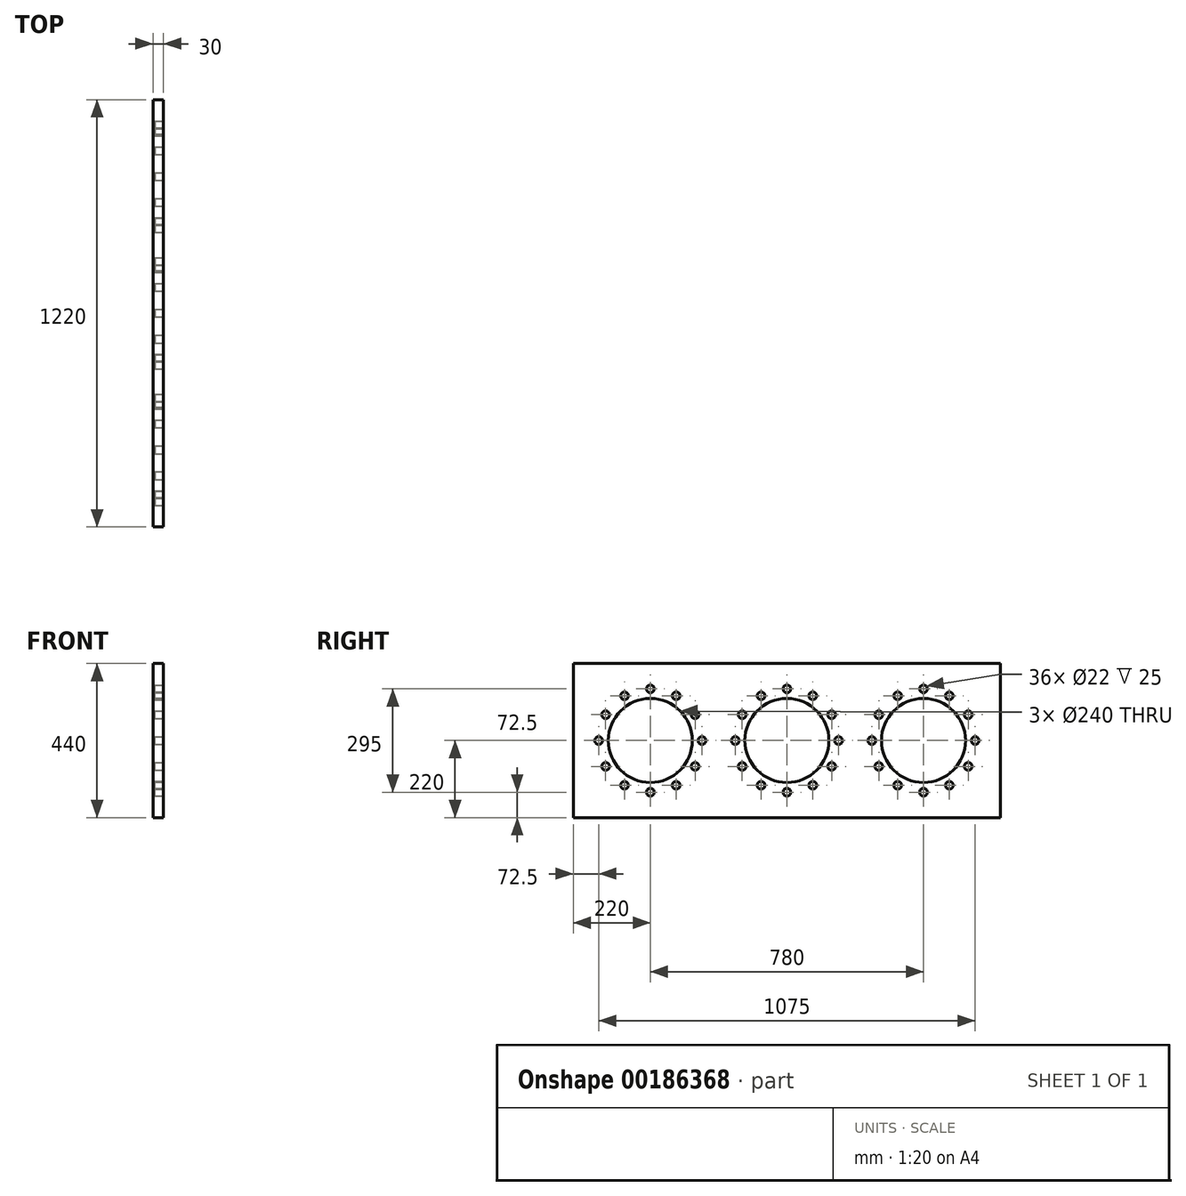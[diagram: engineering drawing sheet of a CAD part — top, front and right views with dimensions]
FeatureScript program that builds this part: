
annotation { "Feature Type Name" : "Feature", "Feature Type Description" : "" }
export const myFeature = defineFeature(function(context is Context, id is Id, definition is map)
    precondition{}
    {
        {
            var Q0;
            Q0=qCreatedBy(makeId("Right.planeOp"),FACE);
            var sketch = newSketch(context, id + "F0", { "sketchPlane" : qUnion([Q0])});
            skCircle(sketch, "E0", {"center": v(610, 220) * mm, "radius": 120 * mm});
            skCircle(sketch, "E1", {"center": v(220, 220) * mm, "radius": 120 * mm});
            skCircle(sketch, "E2", {"center": v(1000, 220) * mm, "radius": 120 * mm});
            skLineSegment(sketch, "E3.bottom", {"start": v(0, 0) * mm, "end": v(1220, 0) * mm});
            skLineSegment(sketch, "E3.top", {"start": v(0, 440) * mm, "end": v(1220, 440) * mm});
            skLineSegment(sketch, "E3.left", {"start": v(0, 0) * mm, "end": v(0, 440) * mm});
            skLineSegment(sketch, "E3.right", {"start": v(1220, 0) * mm, "end": v(1220, 440) * mm});
            skLineSegment(sketch, "E4", {"start": v(0, 220) * mm, "end": v(1220, 220) * mm, "construction": true});
            skSolve(sketch);
        }
        {
            var Q0;
            Q0=makeQuery(id+"F0.imprint","IMPRINT",FACE,{"disambiguationData":[TD([[makeQuery(id+"F0.imprint","IMPRINT",EDGE,{"derivedFrom":sQuery(id+"F0.wireOp",EDGE,"E0")}),-1.0]])]});
            extrude(context, id + "F1", {"entities" : qUnion([Q0]), "depth" : 30 * mm});
        }
        {
            var Q0;
            Q0=makeQuery(id+"F1.opExtrude","CAP_FACE",FACE,{"disambiguationData":[OSD([sQuery(id+"F0.wireOp",EDGE,"E0"),sQuery(id+"F0.wireOp",EDGE,"E1"),sQuery(id+"F0.wireOp",EDGE,"E2"),sQuery(id+"F0.wireOp",EDGE,"E3.bottom"),sQuery(id+"F0.wireOp",EDGE,"E3.top"),sQuery(id+"F0.wireOp",EDGE,"E3.left"),sQuery(id+"F0.wireOp",EDGE,"E3.right")])],"isStart":false});
            var sketch = newSketch(context, id + "F2", { "sketchPlane" : qUnion([Q0])});
            skCircle(sketch, "E5", {"center": v(367.5, 220) * mm, "radius": 11 * mm});
            skCircle(sketch, "E6.1.0", {"center": v(347.74, 146.25) * mm, "radius": 11 * mm});
            skCircle(sketch, "E6.2.0", {"center": v(293.75, 92.26) * mm, "radius": 11 * mm});
            skCircle(sketch, "E6.3.0", {"center": v(220, 72.5) * mm, "radius": 11 * mm});
            skCircle(sketch, "E6.4.0", {"center": v(146.25, 92.26) * mm, "radius": 11 * mm});
            skCircle(sketch, "E6.5.0", {"center": v(92.26, 146.25) * mm, "radius": 11 * mm});
            skCircle(sketch, "E6.6.0", {"center": v(72.5, 220) * mm, "radius": 11 * mm});
            skCircle(sketch, "E6.7.0", {"center": v(92.26, 293.75) * mm, "radius": 11 * mm});
            skCircle(sketch, "E6.8.0", {"center": v(146.25, 347.74) * mm, "radius": 11 * mm});
            skCircle(sketch, "E6.9.0", {"center": v(220, 367.5) * mm, "radius": 11 * mm});
            skCircle(sketch, "E6.10.0", {"center": v(293.75, 347.74) * mm, "radius": 11 * mm});
            skCircle(sketch, "E6.11.0", {"center": v(347.74, 293.75) * mm, "radius": 11 * mm});
            skPoint(sketch, "E6.center", {"position": v(220, 220) * mm});
            skLineSegment(sketch, "E6.anchor1", {"start": v(220, 220) * mm, "end": v(367.5, 220) * mm, "construction": true});
            skLineSegment(sketch, "E6.anchor2", {"start": v(220, 220) * mm, "end": v(347.74, 293.75) * mm, "construction": true});
            skCircle(sketch, "E7", {"center": v(757.5, 220) * mm, "radius": 11 * mm});
            skCircle(sketch, "E8.1.0", {"center": v(737.74, 293.75) * mm, "radius": 11 * mm});
            skCircle(sketch, "E8.2.0", {"center": v(683.75, 347.74) * mm, "radius": 11 * mm});
            skCircle(sketch, "E8.3.0", {"center": v(610, 367.5) * mm, "radius": 11 * mm});
            skCircle(sketch, "E8.4.0", {"center": v(536.25, 347.74) * mm, "radius": 11 * mm});
            skCircle(sketch, "E8.5.0", {"center": v(482.26, 293.75) * mm, "radius": 11 * mm});
            skCircle(sketch, "E8.6.0", {"center": v(462.5, 220) * mm, "radius": 11 * mm});
            skCircle(sketch, "E8.7.0", {"center": v(482.26, 146.25) * mm, "radius": 11 * mm});
            skCircle(sketch, "E8.8.0", {"center": v(536.25, 92.26) * mm, "radius": 11 * mm});
            skCircle(sketch, "E8.9.0", {"center": v(610, 72.5) * mm, "radius": 11 * mm});
            skCircle(sketch, "E8.10.0", {"center": v(683.75, 92.26) * mm, "radius": 11 * mm});
            skCircle(sketch, "E8.11.0", {"center": v(737.74, 146.25) * mm, "radius": 11 * mm});
            skPoint(sketch, "E8.center", {"position": v(610, 220) * mm});
            skLineSegment(sketch, "E9", {"start": v(610, 220) * mm, "end": v(757.5, 220) * mm, "construction": true});
            skCircle(sketch, "E10", {"center": v(1147.5, 220) * mm, "radius": 11 * mm});
            skCircle(sketch, "E11.1.0", {"center": v(1127.74, 293.75) * mm, "radius": 11 * mm});
            skCircle(sketch, "E11.2.0", {"center": v(1073.75, 347.74) * mm, "radius": 11 * mm});
            skCircle(sketch, "E11.3.0", {"center": v(1000, 367.5) * mm, "radius": 11 * mm});
            skCircle(sketch, "E11.4.0", {"center": v(926.25, 347.74) * mm, "radius": 11 * mm});
            skCircle(sketch, "E11.5.0", {"center": v(872.26, 293.75) * mm, "radius": 11 * mm});
            skCircle(sketch, "E11.6.0", {"center": v(852.5, 220) * mm, "radius": 11 * mm});
            skCircle(sketch, "E11.7.0", {"center": v(872.26, 146.25) * mm, "radius": 11 * mm});
            skCircle(sketch, "E11.8.0", {"center": v(926.25, 92.26) * mm, "radius": 11 * mm});
            skCircle(sketch, "E11.9.0", {"center": v(1000, 72.5) * mm, "radius": 11 * mm});
            skCircle(sketch, "E11.10.0", {"center": v(1073.75, 92.26) * mm, "radius": 11 * mm});
            skCircle(sketch, "E11.11.0", {"center": v(1127.74, 146.25) * mm, "radius": 11 * mm});
            skPoint(sketch, "E11.center", {"position": v(1000, 220) * mm});
            skLineSegment(sketch, "E12", {"start": v(1000, 220) * mm, "end": v(1147.5, 220) * mm});
            skSolve(sketch);
        }
        {
            var Q0;
            Q0 = qSketchRegion(id + "F2", true);
            extrude(context, id + "F3", {"entities" : qUnion([Q0]), "operationType" : NewBodyOperationType.REMOVE, "oppositeDirection" : true, "depth" : 25 * mm});
        }
    });
